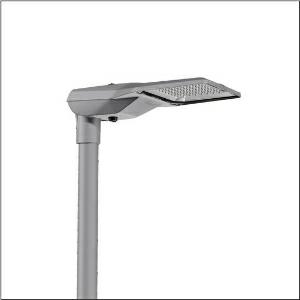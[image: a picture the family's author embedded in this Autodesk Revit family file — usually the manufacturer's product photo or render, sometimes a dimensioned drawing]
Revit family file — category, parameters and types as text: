
# Revit family: streetlight_sl_21_midi___st0_8a_5xe3c33t08nb_d41b
name_source: partatom
category: Lighting Fixtures
units: mm (PartAtom-declared; Revit-internal decimal feet)

## family parameters
Cut with Voids When Loaded = No
Host = Face
Light Source = No
Part Type = Normal
Room Calculation Point = No
Round Connector Dimension = Use Diameter
Shared = No

## types (1)
- --- (1 x LED, 22700 lm, 151.2 W, 3000K)
    Apparent Load = 151 VA
    CIE Flux Codes = 41 75 97 100 100
    Color Rendering = 70
    Color Temperature = 3000K
    Default Elevation = 1800 mm
    Description = Streetlight SL 21 midi, mast luminaire, primary light control with lens, of PMMA, primary optical cover: cover, of toughened safety glass, transparent, light distribution: ST0.8a, light emission: direct distribution, primary light characteristic: asymmetric, installation type: side-entry, post-top, LED, High Power LED, rated luminous flux: 22.700lm, luminous efficacy: 150lm/W, light colour: 730, colour temperature: 3000K, control gear: D4i, control: overheat protection, constant luminous flux control, time-dependent luminous flux control, flexible luminous flux parameterisation, pre-setting: logarithmic dimming characteristic, mains connection: 230..240V, AC, 50/60Hz, start of lifetime: 151W, end of service life: 157W, reduction: 70W, luminaire housing, of diecast aluminium, powder-coated, SITECO metallic grey (DB 702S), corrosivity category C5 high according to DIN EN ISO 12944, please order mast flange separately, inclination adjustable: 0°, 5°, 10°, 15°, sealing non-destructively replaceable, multi-level sealing system, length: 644mm, width: 335mm, height: 110mm, mast flange for spigot size: 42mm (side-entry): 5XC10008XM4, 60/48mm (side-entry/post-top): 5XC10108XM2, 76/60mm (side-entry/post-top): 5XC10108XM1, mounting height: 4..8m, Smart Interface below and above, protection rating (complete): IP66, insulation class (complete): insulation class II (safety insulation), certification: CE, ENEC, ENEC+, VDE, impact resistance: IK10, permissible operating ambient temperature for outdoor applications: -40..+50°C, standard-compliant lighting for roads and squares, packaging unit: 1 piece

Light Distribution: ST0.8a
    Height = 111 mm
    Lamp = 1 x LED
    Lamp Light Flux = 22700 lm
    Lamp Power = 151.2 W
    Lamp count = 1
    Length = 644 mm
    Luminous efficacy = 150 lm/W
    Manufacturer = Siteco
    ModVariant = No
    Model = 5XE3C33T08NB
    Number of Poles = 1
    OnlyDefault = Yes
    Power Factor = 1
    Product Name = Streetlight SL 21 midi | ST0.8a
    Product group = mast luminaire | pylon top
    ProductGroupID = 6100
    Protection Class = Protection class II
    Protection Degree = IP 66
    RLX_Detail_Level = 1
    RLX_Emergency_Light_Flux = 0 lm
    RLX_Emergency_Type = 0
    RLX_Emergency_Type_DB = No
    RlxData = <blob elided: 27101 chars, md5=bd094f10>
    Socket = socket
    Standby Power = 0 W
    System Light Flux = 22700 lm
    System Power = 151 W
    Type Comments = factory setting: luminous flux: 100 % | dim-lin: 254 | 802 mA
    Type Image = l_1004304.jpg
    URL = http://relux.com
    VarID = @adj_168121
    Voltage = 0 V
    Weight = 0.00 kg
    Width = 336 mm

## geometry (parser evidence)
native form markers: Blend x4, Sweep x11
no freeform markers — native parametric forms only
